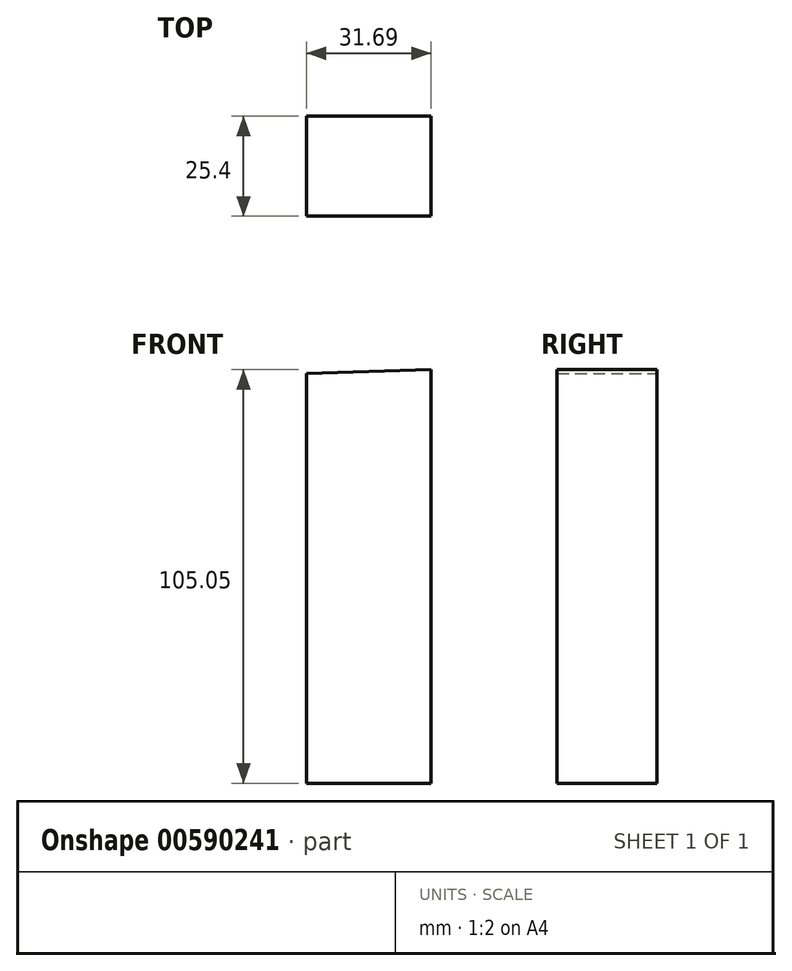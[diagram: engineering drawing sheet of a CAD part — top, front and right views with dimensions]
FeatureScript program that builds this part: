
annotation { "Feature Type Name" : "Feature", "Feature Type Description" : "" }
export const myFeature = defineFeature(function(context is Context, id is Id, definition is map)
    precondition{}
    {
        {
            var Q0;
            Q0=qCreatedBy(makeId("Front.planeOp"),FACE);
            var sketch = newSketch(context, id + "F0", { "sketchPlane" : qUnion([Q0])});
            skLineSegment(sketch, "E0", {"start": v(-66.03, 51.3) * mm, "end": v(-66.03, -52.84) * mm});
            skLineSegment(sketch, "E1", {"start": v(-62.2, -52.84) * mm, "end": v(-34.34, -52.84) * mm});
            skLineSegment(sketch, "E2", {"start": v(-34.34, -52.84) * mm, "end": v(-34.34, 52.21) * mm});
            skLineSegment(sketch, "E3", {"start": v(-34.34, 52.21) * mm, "end": v(-66.03, 51.3) * mm});
            skLineSegment(sketch, "E4", {"start": v(-62.2, -52.84) * mm, "end": v(-66.03, -52.84) * mm});
            skSolve(sketch);
        }
        {
            var Q0;
            Q0=makeQuery(id+"F0.imprint","IMPRINT",FACE,{"disambiguationData":[TD([[makeQuery(id+"F0.imprint","IMPRINT",EDGE,{"derivedFrom":sQuery(id+"F0.wireOp",EDGE,"E0")}),1.0]])]});
            extrude(context, id + "F1", {"entities" : qUnion([Q0]), "depth" : 25.4 * mm, "offsetDistance" : 25.4 * mm});
        }
    });
